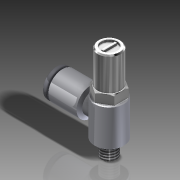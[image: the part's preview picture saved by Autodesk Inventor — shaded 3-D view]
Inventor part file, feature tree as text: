
AUTODESK INVENTOR PART (.ipt)
format: ipt  version: 2011 (Build 150239000, 239)  size: 216,576 bytes
history: native  units: in
note: dims shown in document units (in); Inventor stores cm internally (conversion verified against a paired STEP export)
features: other x1, imported_body x1, thread x1
ambient origin geometry x8: Origin, YZ Plane, XZ Plane, XY Plane, X Axis, Y Axis, Z Axis, Center Point
feature tree (3):
  parser-record x1  (decoder bookkeeping rows leaked as tree rows — omitted from the tree; the rows remain in map.json)
  imported_body  "Base1"
  thread  "Thread1"  [1 undecoded]
note: 1 required parameter value undecoded (feature->parameter linkage not recoverable at this tier; creation-order binding heuristic only, values carry confidence <= 0.55)
